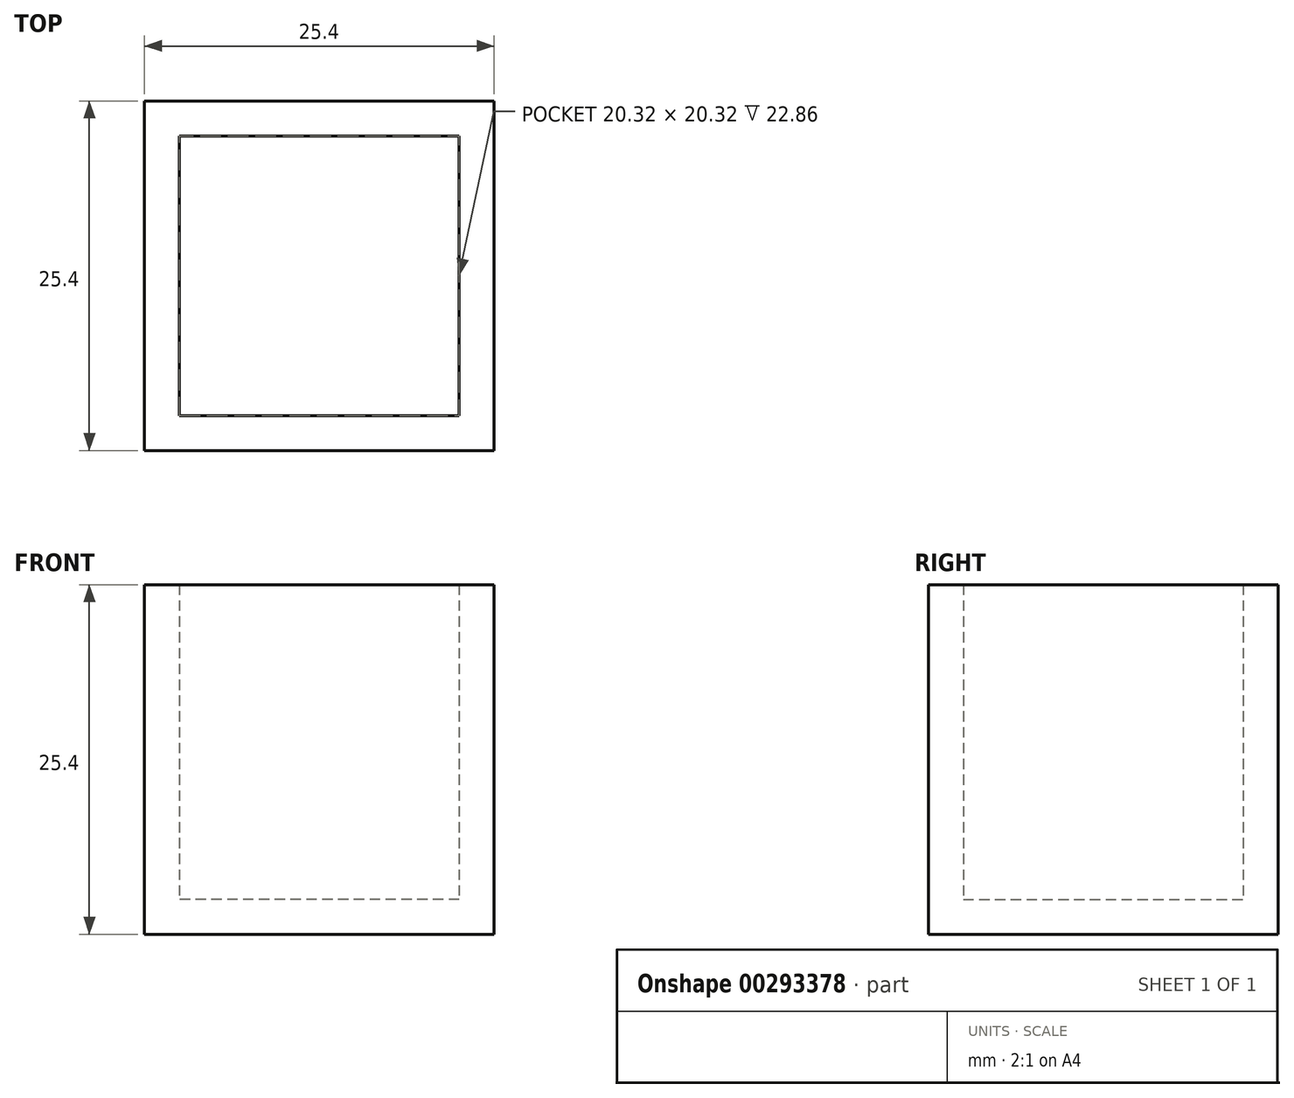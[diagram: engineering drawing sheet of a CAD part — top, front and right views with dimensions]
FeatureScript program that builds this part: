
annotation { "Feature Type Name" : "Feature", "Feature Type Description" : "" }
export const myFeature = defineFeature(function(context is Context, id is Id, definition is map)
    precondition{}
    {
        {
            var Q0;
            Q0=qCreatedBy(makeId("Front.planeOp"),FACE);
            var sketch = newSketch(context, id + "F0", { "sketchPlane" : qUnion([Q0])});
            skLineSegment(sketch, "E0.bottom", {"start": v(12.7, 12.7) * mm, "end": v(-12.7, 12.7) * mm});
            skLineSegment(sketch, "E0.top", {"start": v(12.7, -12.7) * mm, "end": v(-12.7, -12.7) * mm});
            skLineSegment(sketch, "E0.left", {"start": v(12.7, 12.7) * mm, "end": v(12.7, -12.7) * mm});
            skLineSegment(sketch, "E0.right", {"start": v(-12.7, 12.7) * mm, "end": v(-12.7, -12.7) * mm});
            skPoint(sketch, "E0.middle", {"position": v(0, 0) * mm});
            skSolve(sketch);
        }
        {
            var Q0;
            Q0=makeQuery(id+"F0.imprint","IMPRINT",FACE,{"disambiguationData":[TD([[makeQuery(id+"F0.imprint","IMPRINT",EDGE,{"derivedFrom":sQuery(id+"F0.wireOp",EDGE,"E0.bottom")}),1.0]])]});
            extrude(context, id + "F1", {"entities" : qUnion([Q0]), "depth" : 25.4 * mm});
        }
        {
            var Q0;
            Q0=makeQuery(id+"F1.opExtrude","SWEPT_FACE",FACE,{"disambiguationData":[OSD([sQuery(id+"F0.wireOp",EDGE,"E0.bottom")])]});
            shell(context, id + "F2", {"entities" : qUnion([Q0]), "thickness" : 2.54 * mm});
        }
        {
            var Q0;
            Q0=makeQuery(id+"F1.opExtrude","SWEPT_BODY",BODY,{"disambiguationData":[OSD([sQuery(id+"F0.wireOp",EDGE,"E0.bottom"),sQuery(id+"F0.wireOp",EDGE,"E0.top"),sQuery(id+"F0.wireOp",EDGE,"E0.left"),sQuery(id+"F0.wireOp",EDGE,"E0.right")])]});
            transform(context, id + "F3", {"entities" : qUnion([Q0]), "transformType" : TransformType.TRANSLATION_3D, "dx" : 0 * mm, "dy" : 0 * mm, "dz" : 0 * mm, "makeCopy" : true});
        }
        {
            var Q0;
            Q0=makeQuery(id+"F3.opPattern","COPY",BODY,{"derivedFrom":makeQuery(id+"F1.opExtrude","SWEPT_BODY",BODY,{"disambiguationData":[OSD([sQuery(id+"F0.wireOp",EDGE,"E0.bottom"),sQuery(id+"F0.wireOp",EDGE,"E0.top"),sQuery(id+"F0.wireOp",EDGE,"E0.left"),sQuery(id+"F0.wireOp",EDGE,"E0.right")])]}),"instanceName":"1"});
            deleteBodies(context, id + "F4", {"entities" : qUnion([Q0])});
        }
    });
